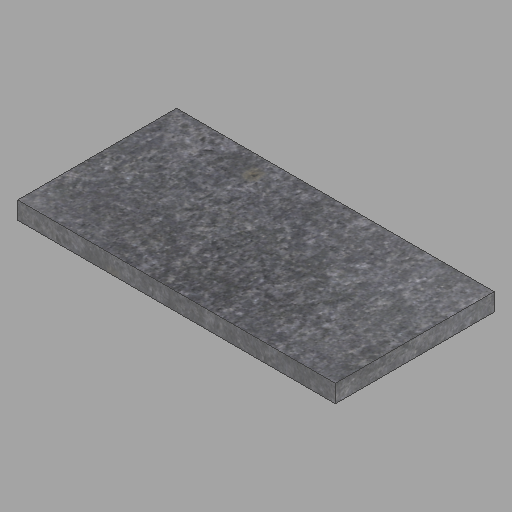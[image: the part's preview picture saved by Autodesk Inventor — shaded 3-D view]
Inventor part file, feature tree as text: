
AUTODESK INVENTOR PART (.ipt)
format: ipt  version: 2023 (Build 270158000, 158)  size: 229,888 bytes
history: native  units: in
note: dims shown in document units (in); Inventor stores cm internally (conversion verified against a paired STEP export)
features: other x1, extrude x1, sketch x1
ambient origin geometry x8: Origin, YZ Plane, XZ Plane, XY Plane, X Axis, Y Axis, Z Axis, Center Point
bodies: Solid1 (feature_tree)
feature tree (3):
  other  "2x18x36-34"
  extrude  "Extrusion1"  Depth=18.0in
  sketch  "Sketch1"  dims[d0=2.0in d1=18.0in d2=36.0in d3=0.0in]
